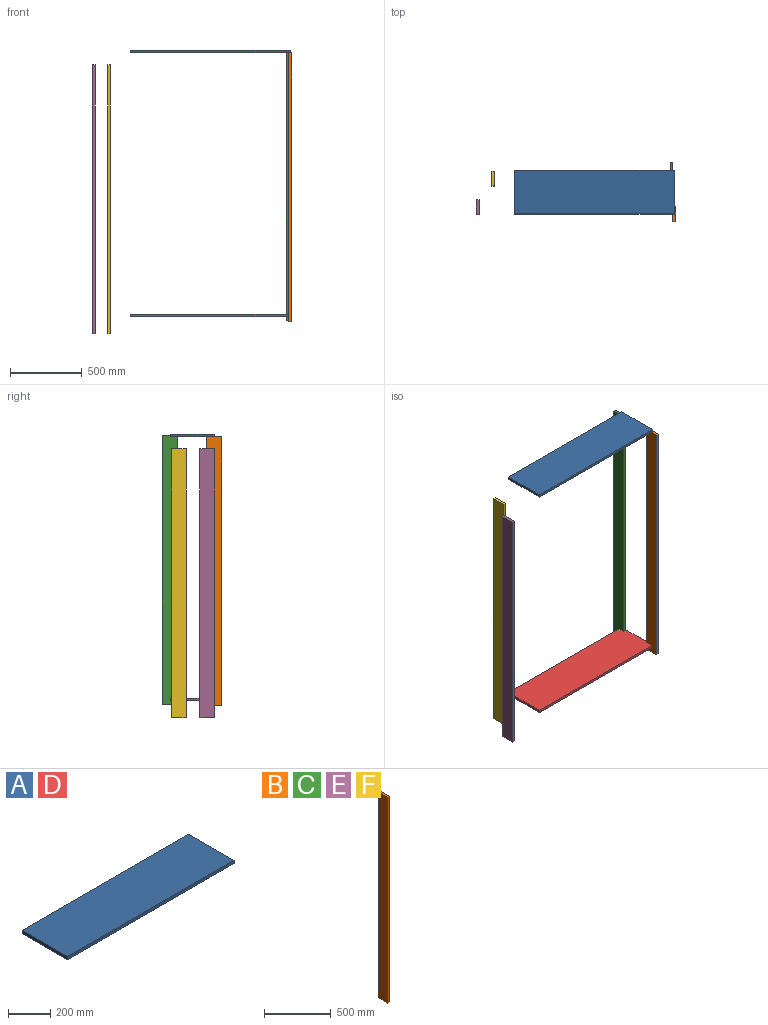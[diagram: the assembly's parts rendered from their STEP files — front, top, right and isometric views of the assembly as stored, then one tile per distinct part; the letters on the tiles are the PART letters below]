
ASSEMBLY  parts=6 mates=1
PART A: 6 faces, bbox 1117.6x304.8x19.1 mm
  f0: plane 1117.6x19.05mm, normal (0,-1,0), area 21290.3mm2, adj f1,f3,f4,f5
  f1: plane 304.8x19.05mm, normal (1,0,0), area 5806.4mm2, adj f0,f2,f4,f5
  f2: plane 1117.6x19.05mm, normal (0,1,0), area 21290.3mm2, adj f1,f3,f4,f5
  f3: plane 304.8x19.05mm, normal (-1,0,0), area 5806.4mm2, adj f0,f2,f4,f5
  f4: plane 1117.6x304.8mm, normal (0,0,1), area 340644.5mm2, adj f0,f1,f2,f3
  f5: plane 1117.6x304.8mm, normal (0,0,-1), area 340644.5mm2, adj f0,f1,f2,f3
PART B: 6 faces, bbox 19.1x101.6x1879.6 mm
  f0: plane 1879.6x19.05mm, normal (0,-1,0), area 35806.4mm2, adj f1,f3,f4,f5
  f1: plane 101.6x19.05mm, normal (0,0,-1), area 1935.5mm2, adj f0,f2,f4,f5
  f2: plane 1879.6x19.05mm, normal (0,1,0), area 35806.4mm2, adj f1,f3,f4,f5
  f3: plane 101.6x19.05mm, normal (0,0,1), area 1935.5mm2, adj f0,f2,f4,f5
  f4: plane 1879.6x101.6mm, normal (1,0,0), area 190967.4mm2, adj f0,f1,f2,f3
  f5: plane 1879.6x101.6mm, normal (-1,0,0), area 190967.4mm2, adj f0,f1,f2,f3
PART C: same geometry as B
PART D: same geometry as A
PART E: same geometry as B
PART F: same geometry as B
PLACE A t=(-2.73,-437.2,1023.27)mm
PLACE B t=(668.94,-572.43,83.47)mm
PLACE C t=(650.24,-261.62,93.98)mm
PLACE D t=(-2.73,-437.2,-821.41)mm fixed
PLACE E t=(-703.58,-523.24,0)mm
PLACE F t=(-596.9,-325.12,0)mm
MATE fastened B.f3 <-> A.f5  axis (0,0,1) through (678.46,-572.43,1023.27)mm
